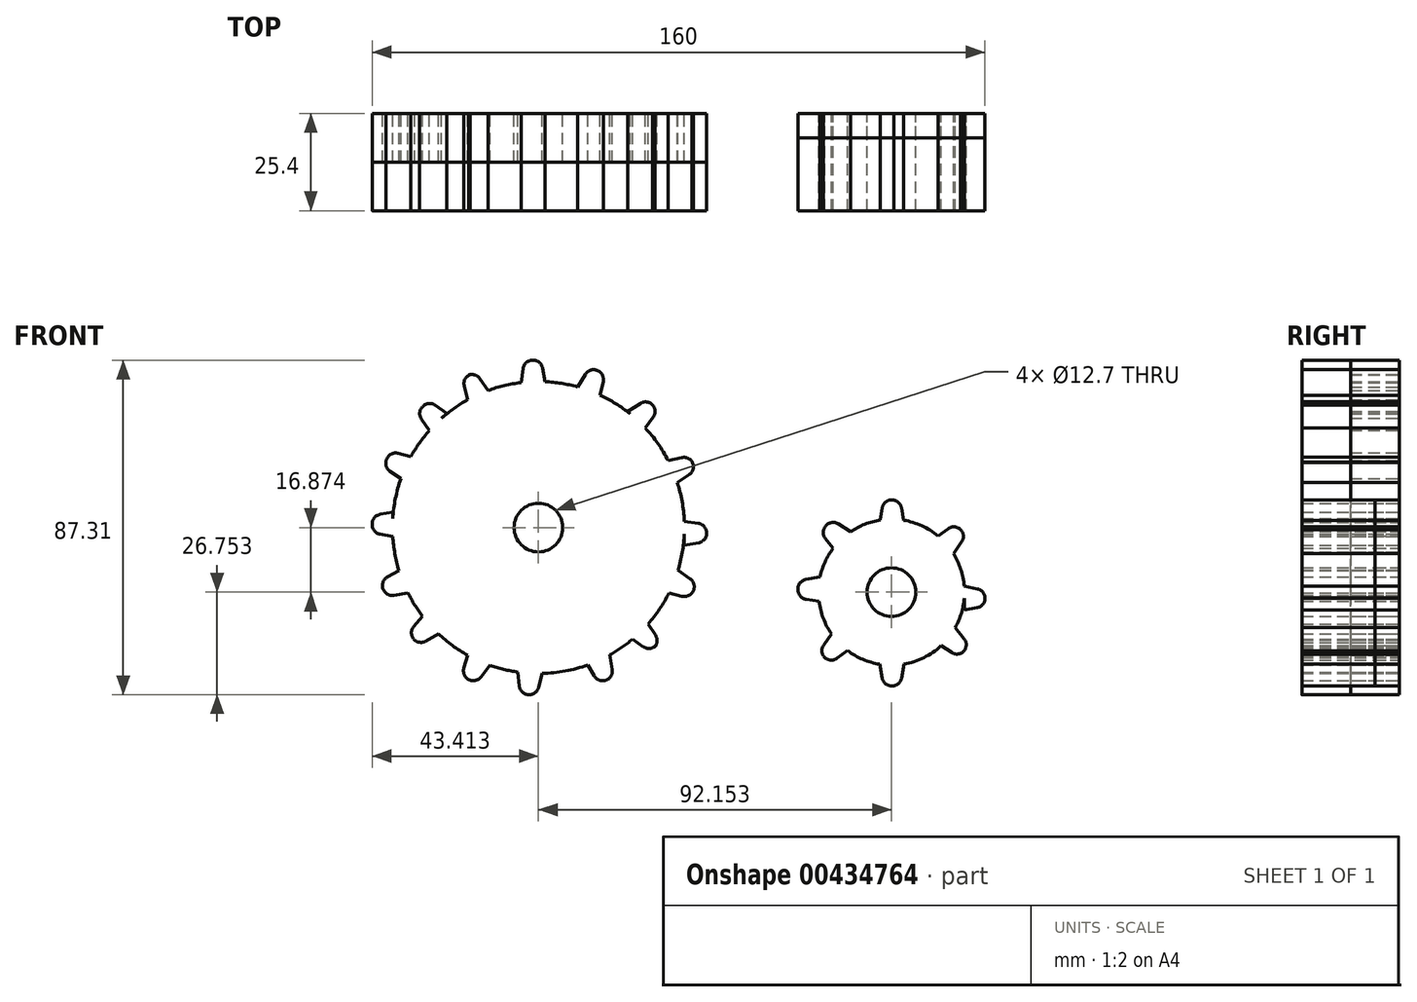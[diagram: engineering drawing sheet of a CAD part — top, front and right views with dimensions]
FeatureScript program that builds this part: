
annotation { "Feature Type Name" : "Feature", "Feature Type Description" : "" }
export const myFeature = defineFeature(function(context is Context, id is Id, definition is map)
    precondition{}
    {
        {
            var Q0;
            Q0=qCreatedBy(makeId("Front.planeOp"),FACE);
            var sketch = newSketch(context, id + "F0", { "sketchPlane" : qUnion([Q0])});
            skCircle(sketch, "E0", {"center": v(-53.1, 42.78) * mm, "radius": 38.1 * mm});
            skCircle(sketch, "E1", {"center": v(-53.1, 42.78) * mm, "radius": 6.35 * mm});
            skLineSegment(sketch, "E2", {"start": v(-57.08, 84.31) * mm, "end": v(-57.66, 80.6) * mm});
            skLineSegment(sketch, "E3", {"start": v(-51.35, 80.6) * mm, "end": v(-52.02, 84.36) * mm});
            skLineSegment(sketch, "E4", {"start": v(-54.55, 86.46) * mm, "end": v(-54.6, 86.46) * mm});
            skLineSegment(sketch, "E5", {"start": v(-57.66, 80.6) * mm, "end": v(-51.35, 80.6) * mm});
            skArc(sketch, "E6.filletArc", {"start": v(-54.6, 86.46) * mm, "mid": v(-56.23, 85.84) * mm, "end": v(-57.08, 84.31) * mm});
            skArc(sketch, "E7.filletArc", {"start": v(-52.02, 84.36) * mm, "mid": v(-52.9, 85.87) * mm, "end": v(-54.55, 86.46) * mm});
            skLineSegment(sketch, "E8", {"start": v(-94.4, 41.03) * mm, "end": v(-91.13, 40.45) * mm});
            skLineSegment(sketch, "E9", {"start": v(-91.13, 46.81) * mm, "end": v(-94.39, 46.24) * mm});
            skLineSegment(sketch, "E10", {"start": v(-96.48, 43.97) * mm, "end": v(-96.5, 43.77) * mm});
            skLineSegment(sketch, "E11", {"start": v(-91.13, 40.45) * mm, "end": v(-91.13, 46.81) * mm});
            skPoint(sketch, "E12.visualSharp", {"position": v(-96.71, 41.44) * mm});
            skArc(sketch, "E12.filletArc", {"start": v(-96.5, 43.77) * mm, "mid": v(-95.99, 42) * mm, "end": v(-94.4, 41.03) * mm});
            skPoint(sketch, "E13.visualSharp", {"position": v(-96.3, 45.9) * mm});
            skArc(sketch, "E13.filletArc", {"start": v(-94.39, 46.24) * mm, "mid": v(-95.81, 45.46) * mm, "end": v(-96.48, 43.97) * mm});
            skLineSegment(sketch, "E14", {"start": v(-26.55, 75.15) * mm, "end": v(-29.77, 73.06) * mm});
            skLineSegment(sketch, "E15", {"start": v(-25.48, 68.46) * mm, "end": v(-23.17, 71.52) * mm});
            skLineSegment(sketch, "E16", {"start": v(-23.33, 74.77) * mm, "end": v(-23.36, 74.8) * mm});
            skLineSegment(sketch, "E17", {"start": v(-29.77, 73.06) * mm, "end": v(-25.48, 68.46) * mm});
            skPoint(sketch, "E18.visualSharp", {"position": v(-24.78, 76.3) * mm});
            skArc(sketch, "E18.filletArc", {"start": v(-23.33, 74.77) * mm, "mid": v(-24.87, 75.54) * mm, "end": v(-26.55, 75.15) * mm});
            skPoint(sketch, "E19.visualSharp", {"position": v(-21.87, 73.25) * mm});
            skArc(sketch, "E19.filletArc", {"start": v(-23.17, 71.52) * mm, "mid": v(-22.66, 73.2) * mm, "end": v(-23.36, 74.8) * mm});
            skLineSegment(sketch, "E20", {"start": v(-82.5, 13.14) * mm, "end": v(-79.21, 15.04) * mm});
            skLineSegment(sketch, "E21", {"start": v(-83.24, 19.83) * mm, "end": v(-85.67, 16.93) * mm});
            skLineSegment(sketch, "E22", {"start": v(-85.44, 13.43) * mm, "end": v(-85.4, 13.39) * mm});
            skLineSegment(sketch, "E23", {"start": v(-79.21, 15.04) * mm, "end": v(-83.24, 19.83) * mm});
            skPoint(sketch, "E24.visualSharp", {"position": v(-84.07, 12.23) * mm});
            skArc(sketch, "E24.filletArc", {"start": v(-85.44, 13.43) * mm, "mid": v(-84.02, 12.81) * mm, "end": v(-82.5, 13.14) * mm});
            skPoint(sketch, "E25.visualSharp", {"position": v(-87.27, 15.03) * mm});
            skArc(sketch, "E25.filletArc", {"start": v(-85.67, 16.93) * mm, "mid": v(-86.25, 15.1) * mm, "end": v(-85.4, 13.39) * mm});
            skLineSegment(sketch, "E26", {"start": v(-15, 42.08) * mm, "end": v(-15, 41.4) * mm});
            skLineSegment(sketch, "E27", {"start": v(-83.64, 71.06) * mm, "end": v(-81.57, 68.1) * mm});
            skLineSegment(sketch, "E28", {"start": v(-77.06, 72.6) * mm, "end": v(-80.03, 74.68) * mm});
            skLineSegment(sketch, "E29", {"start": v(-83.3, 74.37) * mm, "end": v(-83.38, 74.3) * mm});
            skLineSegment(sketch, "E30", {"start": v(-81.57, 68.1) * mm, "end": v(-77.06, 72.6) * mm});
            skPoint(sketch, "E31.visualSharp", {"position": v(-84.85, 72.79) * mm});
            skArc(sketch, "E31.filletArc", {"start": v(-83.38, 74.3) * mm, "mid": v(-84.1, 72.72) * mm, "end": v(-83.64, 71.06) * mm});
            skPoint(sketch, "E32.visualSharp", {"position": v(-81.8, 75.91) * mm});
            skArc(sketch, "E32.filletArc", {"start": v(-80.03, 74.68) * mm, "mid": v(-81.72, 75.12) * mm, "end": v(-83.3, 74.37) * mm});
            skLineSegment(sketch, "E33", {"start": v(-22.56, 14.73) * mm, "end": v(-24.51, 17.59) * mm});
            skLineSegment(sketch, "E34", {"start": v(-28.51, 13.67) * mm, "end": v(-25.72, 11.67) * mm});
            skLineSegment(sketch, "E35", {"start": v(-22.81, 11.55) * mm, "end": v(-22.4, 12) * mm});
            skLineSegment(sketch, "E36", {"start": v(-24.51, 17.59) * mm, "end": v(-28.51, 13.67) * mm});
            skPoint(sketch, "E37.visualSharp", {"position": v(-21.4, 13.04) * mm});
            skArc(sketch, "E37.filletArc", {"start": v(-22.81, 11.55) * mm, "mid": v(-22.13, 13.1) * mm, "end": v(-22.56, 14.73) * mm});
            skPoint(sketch, "E38.visualSharp", {"position": v(-23.92, 10.38) * mm});
            skArc(sketch, "E38.filletArc", {"start": v(-25.72, 11.67) * mm, "mid": v(-24, 11.2) * mm, "end": v(-22.4, 12) * mm});
            skLineSegment(sketch, "E39", {"start": v(-40.85, 82.78) * mm, "end": v(-42.9, 79.49) * mm});
            skLineSegment(sketch, "E40", {"start": v(-37.01, 77.1) * mm, "end": v(-36.2, 80.9) * mm});
            skLineSegment(sketch, "E41", {"start": v(-37.76, 83.79) * mm, "end": v(-37.77, 83.8) * mm});
            skLineSegment(sketch, "E42", {"start": v(-42.9, 79.49) * mm, "end": v(-37.01, 77.1) * mm});
            skPoint(sketch, "E43.visualSharp", {"position": v(-39.73, 84.56) * mm});
            skArc(sketch, "E43.filletArc", {"start": v(-37.77, 83.8) * mm, "mid": v(-39.5, 83.84) * mm, "end": v(-40.85, 82.78) * mm});
            skPoint(sketch, "E44.visualSharp", {"position": v(-35.75, 83) * mm});
            skArc(sketch, "E44.filletArc", {"start": v(-36.2, 80.9) * mm, "mid": v(-36.45, 82.62) * mm, "end": v(-37.76, 83.79) * mm});
            skPoint(sketch, "E45.endSnap0", {"position": v(-92.76, 46.52) * mm});
            skLineSegment(sketch, "E46", {"start": v(-68.07, 3.83) * mm, "end": v(-65.78, 6.85) * mm});
            skLineSegment(sketch, "E47", {"start": v(-71.45, 9.76) * mm, "end": v(-72.57, 6.13) * mm});
            skLineSegment(sketch, "E48", {"start": v(-71.13, 3.05) * mm, "end": v(-71.09, 3.03) * mm});
            skLineSegment(sketch, "E49", {"start": v(-65.78, 6.85) * mm, "end": v(-71.45, 9.76) * mm});
            skPoint(sketch, "E50.visualSharp", {"position": v(-69.27, 2.25) * mm});
            skArc(sketch, "E50.filletArc", {"start": v(-71.09, 3.03) * mm, "mid": v(-69.44, 2.9) * mm, "end": v(-68.07, 3.83) * mm});
            skPoint(sketch, "E51.visualSharp", {"position": v(-73.25, 3.94) * mm});
            skArc(sketch, "E51.filletArc", {"start": v(-72.57, 6.13) * mm, "mid": v(-72.45, 4.31) * mm, "end": v(-71.13, 3.05) * mm});
            skLineSegment(sketch, "E52", {"start": v(-33.84, 5.77) * mm, "end": v(-34.5, 9.53) * mm});
            skLineSegment(sketch, "E53", {"start": v(-40.44, 7.36) * mm, "end": v(-38.54, 4.06) * mm});
            skLineSegment(sketch, "E54", {"start": v(-35.44, 2.95) * mm, "end": v(-35.44, 2.95) * mm});
            skLineSegment(sketch, "E55", {"start": v(-34.5, 9.53) * mm, "end": v(-40.44, 7.36) * mm});
            skPoint(sketch, "E56.visualSharp", {"position": v(-33.47, 3.7) * mm});
            skArc(sketch, "E56.filletArc", {"start": v(-35.44, 2.95) * mm, "mid": v(-34.13, 4.07) * mm, "end": v(-33.84, 5.77) * mm});
            skPoint(sketch, "E57.visualSharp", {"position": v(-37.46, 2.2) * mm});
            skArc(sketch, "E57.filletArc", {"start": v(-38.54, 4.06) * mm, "mid": v(-37.2, 2.94) * mm, "end": v(-35.44, 2.95) * mm});
            skLineSegment(sketch, "E58", {"start": v(-72.47, 79.7) * mm, "end": v(-71.54, 76.12) * mm});
            skLineSegment(sketch, "E59", {"start": v(-66.26, 78.53) * mm, "end": v(-68.39, 81.61) * mm});
            skLineSegment(sketch, "E60", {"start": v(-70.88, 82.73) * mm, "end": v(-71.35, 82.55) * mm});
            skLineSegment(sketch, "E61", {"start": v(-71.54, 76.12) * mm, "end": v(-66.26, 78.53) * mm});
            skPoint(sketch, "E62.visualSharp", {"position": v(-73.05, 81.93) * mm});
            skArc(sketch, "E62.filletArc", {"start": v(-70.88, 82.73) * mm, "mid": v(-72.26, 81.52) * mm, "end": v(-72.47, 79.7) * mm});
            skPoint(sketch, "E63.visualSharp", {"position": v(-69.5, 83.23) * mm});
            skArc(sketch, "E63.filletArc", {"start": v(-68.39, 81.61) * mm, "mid": v(-69.7, 82.59) * mm, "end": v(-71.35, 82.55) * mm});
            skLineSegment(sketch, "E64", {"start": v(-91.88, 57.5) * mm, "end": v(-89.01, 55.5) * mm});
            skLineSegment(sketch, "E65", {"start": v(-86.33, 61.25) * mm, "end": v(-89.7, 62.15) * mm});
            skLineSegment(sketch, "E66", {"start": v(-92.68, 60.75) * mm, "end": v(-92.73, 60.62) * mm});
            skLineSegment(sketch, "E67", {"start": v(-89.01, 55.5) * mm, "end": v(-86.33, 61.25) * mm});
            skPoint(sketch, "E68.visualSharp", {"position": v(-93.6, 58.7) * mm});
            skArc(sketch, "E68.filletArc", {"start": v(-92.73, 60.62) * mm, "mid": v(-92.87, 58.9) * mm, "end": v(-91.88, 57.5) * mm});
            skPoint(sketch, "E69.visualSharp", {"position": v(-91.79, 62.7) * mm});
            skArc(sketch, "E69.filletArc", {"start": v(-89.7, 62.15) * mm, "mid": v(-91.45, 62) * mm, "end": v(-92.68, 60.75) * mm});
            skLineSegment(sketch, "E70", {"start": v(-13.52, 29.42) * mm, "end": v(-16.67, 31.62) * mm});
            skLineSegment(sketch, "E71", {"start": v(-19.36, 25.84) * mm, "end": v(-15.65, 24.85) * mm});
            skLineSegment(sketch, "E72", {"start": v(-12.68, 26.25) * mm, "end": v(-12.66, 26.29) * mm});
            skLineSegment(sketch, "E73", {"start": v(-16.67, 31.62) * mm, "end": v(-19.36, 25.84) * mm});
            skPoint(sketch, "E74.visualSharp", {"position": v(-11.8, 28.2) * mm});
            skArc(sketch, "E74.filletArc", {"start": v(-12.66, 26.29) * mm, "mid": v(-12.53, 28) * mm, "end": v(-13.52, 29.42) * mm});
            skPoint(sketch, "E75.visualSharp", {"position": v(-13.57, 24.3) * mm});
            skArc(sketch, "E75.filletArc", {"start": v(-15.65, 24.85) * mm, "mid": v(-13.9, 25) * mm, "end": v(-12.68, 26.25) * mm});
            skLineSegment(sketch, "E76", {"start": v(-90.84, 25.08) * mm, "end": v(-87.15, 25.7) * mm});
            skLineSegment(sketch, "E77", {"start": v(-89.27, 31.68) * mm, "end": v(-92.52, 29.85) * mm});
            skLineSegment(sketch, "E78", {"start": v(-93.57, 26.53) * mm, "end": v(-93.54, 26.49) * mm});
            skLineSegment(sketch, "E79", {"start": v(-87.15, 25.7) * mm, "end": v(-89.27, 31.68) * mm});
            skPoint(sketch, "E80.visualSharp", {"position": v(-92.72, 24.77) * mm});
            skArc(sketch, "E80.filletArc", {"start": v(-93.54, 26.49) * mm, "mid": v(-92.42, 25.33) * mm, "end": v(-90.84, 25.08) * mm});
            skPoint(sketch, "E81.visualSharp", {"position": v(-94.6, 28.68) * mm});
            skArc(sketch, "E81.filletArc", {"start": v(-92.52, 29.85) * mm, "mid": v(-93.7, 28.4) * mm, "end": v(-93.57, 26.53) * mm});
            skLineSegment(sketch, "E82", {"start": v(-15.68, 61.02) * mm, "end": v(-19.23, 60.23) * mm});
            skLineSegment(sketch, "E83", {"start": v(-16.86, 54.56) * mm, "end": v(-13.82, 56.51) * mm});
            skLineSegment(sketch, "E84", {"start": v(-12.92, 59.79) * mm, "end": v(-12.98, 59.9) * mm});
            skLineSegment(sketch, "E85", {"start": v(-19.23, 60.23) * mm, "end": v(-16.86, 54.56) * mm});
            skPoint(sketch, "E86.visualSharp", {"position": v(-13.84, 61.43) * mm});
            skArc(sketch, "E86.filletArc", {"start": v(-12.92, 59.79) * mm, "mid": v(-14.1, 60.86) * mm, "end": v(-15.68, 61.02) * mm});
            skPoint(sketch, "E87.visualSharp", {"position": v(-11.8, 57.8) * mm});
            skArc(sketch, "E87.filletArc", {"start": v(-13.82, 56.51) * mm, "mid": v(-12.72, 58.04) * mm, "end": v(-12.98, 59.9) * mm});
            skLineSegment(sketch, "E88", {"start": v(-11.34, 43.85) * mm, "end": v(-15.03, 44.44) * mm});
            skLineSegment(sketch, "E89", {"start": v(-15.03, 38.13) * mm, "end": v(-11.3, 38.8) * mm});
            skLineSegment(sketch, "E90", {"start": v(-9.2, 41.32) * mm, "end": v(-9.2, 41.37) * mm});
            skLineSegment(sketch, "E91", {"start": v(-15.03, 44.44) * mm, "end": v(-15.03, 38.13) * mm});
            skArc(sketch, "E92.filletArc", {"start": v(-9.2, 41.37) * mm, "mid": v(-9.81, 43) * mm, "end": v(-11.34, 43.85) * mm});
            skArc(sketch, "E93.filletArc", {"start": v(-11.3, 38.8) * mm, "mid": v(-9.78, 39.67) * mm, "end": v(-9.2, 41.32) * mm});
            skLineSegment(sketch, "E94", {"start": v(-53.07, 1.08) * mm, "end": v(-52.18, 4.69) * mm});
            skLineSegment(sketch, "E95", {"start": v(-58.45, 5.24) * mm, "end": v(-58.12, 1.48) * mm});
            skLineSegment(sketch, "E96", {"start": v(-55.78, -0.84) * mm, "end": v(-55.73, -0.84) * mm});
            skLineSegment(sketch, "E97", {"start": v(-52.18, 4.69) * mm, "end": v(-58.45, 5.24) * mm});
            skArc(sketch, "E98.filletArc", {"start": v(-55.73, -0.84) * mm, "mid": v(-54.05, -0.37) * mm, "end": v(-53.07, 1.08) * mm});
            skArc(sketch, "E99.filletArc", {"start": v(-58.12, 1.48) * mm, "mid": v(-57.38, -0.1) * mm, "end": v(-55.78, -0.84) * mm});
            skSolve(sketch);
        }
        {
            var Q0;
            Q0 = qSketchRegion(id + "F0", true);
            extrude(context, id + "F1", {"entities" : qUnion([Q0]), "depth" : 12.7 * mm});
        }
        {
            var Q0;
            Q0=qCreatedBy(makeId("Front.planeOp"),FACE);
            var sketch = newSketch(context, id + "F2", { "sketchPlane" : qUnion([Q0])});
            skCircle(sketch, "E100", {"center": v(39.06, 25.9) * mm, "radius": 19.05 * mm});
            skCircle(sketch, "E101", {"center": v(39.06, 25.9) * mm, "radius": 6.35 * mm});
            skLineSegment(sketch, "E102", {"start": v(36.67, 47.92) * mm, "end": v(36.09, 44.72) * mm});
            skLineSegment(sketch, "E103", {"start": v(42.2, 44.7) * mm, "end": v(41.66, 47.9) * mm});
            skLineSegment(sketch, "E104", {"start": v(39.73, 49.94) * mm, "end": v(39.72, 49.95) * mm});
            skLineSegment(sketch, "E105", {"start": v(36.09, 44.72) * mm, "end": v(42.2, 44.7) * mm});
            skArc(sketch, "E106.filletArc", {"start": v(39.73, 49.94) * mm, "mid": v(37.77, 49.59) * mm, "end": v(36.67, 47.92) * mm});
            skPoint(sketch, "E107.visualSharp", {"position": v(40.78, 63.59) * mm});
            skArc(sketch, "E107.filletArc", {"start": v(41.66, 47.9) * mm, "mid": v(41, 49.22) * mm, "end": v(39.72, 49.95) * mm});
            skLineSegment(sketch, "E108", {"start": v(41.69, 3.54) * mm, "end": v(42.3, 7.13) * mm});
            skLineSegment(sketch, "E109", {"start": v(36, 7.1) * mm, "end": v(36.64, 3.52) * mm});
            skLineSegment(sketch, "E110", {"start": v(38.9, 1.44) * mm, "end": v(38.95, 1.44) * mm});
            skLineSegment(sketch, "E111", {"start": v(42.3, 7.13) * mm, "end": v(36, 7.1) * mm});
            skPoint(sketch, "E112.visualSharp", {"position": v(41.3, 1.23) * mm});
            skArc(sketch, "E112.filletArc", {"start": v(38.95, 1.44) * mm, "mid": v(40.73, 1.96) * mm, "end": v(41.69, 3.54) * mm});
            skPoint(sketch, "E113.visualSharp", {"position": v(36.98, 1.62) * mm});
            skArc(sketch, "E113.filletArc", {"start": v(36.64, 3.52) * mm, "mid": v(37.42, 2.1) * mm, "end": v(38.9, 1.44) * mm});
            skLineSegment(sketch, "E114", {"start": v(36, 7.1) * mm, "end": v(39.06, 7.49) * mm});
            skLineSegment(sketch, "E115", {"start": v(39.06, 25.9) * mm, "end": v(39.06, 21.65) * mm});
            skLineSegment(sketch, "E116", {"start": v(39.06, 25.9) * mm, "end": v(39.06, 30.09) * mm});
            skLineSegment(sketch, "E117", {"start": v(4.99, 41.49) * mm, "end": v(9.44, 41.49) * mm});
            skLineSegment(sketch, "E118", {"start": v(17.84, 46.87) * mm, "end": v(22.3, 46.87) * mm});
            skLineSegment(sketch, "E119", {"start": v(16.79, 24.04) * mm, "end": v(20.49, 23.45) * mm});
            skLineSegment(sketch, "E120", {"start": v(20.49, 29.9) * mm, "end": v(16.74, 29.23) * mm});
            skLineSegment(sketch, "E121", {"start": v(14.64, 26.7) * mm, "end": v(14.64, 26.52) * mm});
            skLineSegment(sketch, "E122", {"start": v(20.49, 23.45) * mm, "end": v(20.49, 29.9) * mm});
            skArc(sketch, "E123.filletArc", {"start": v(14.64, 26.52) * mm, "mid": v(15.26, 24.89) * mm, "end": v(16.79, 24.04) * mm});
            skArc(sketch, "E124.filletArc", {"start": v(16.74, 29.23) * mm, "mid": v(15.22, 28.35) * mm, "end": v(14.64, 26.7) * mm});
            skLineSegment(sketch, "E125", {"start": v(61.47, 26.78) * mm, "end": v(58.04, 27.5) * mm});
            skLineSegment(sketch, "E126", {"start": v(58.04, 21.26) * mm, "end": v(61.39, 21.85) * mm});
            skLineSegment(sketch, "E127", {"start": v(63.49, 24.32) * mm, "end": v(63.49, 24.38) * mm});
            skLineSegment(sketch, "E128", {"start": v(58.04, 27.5) * mm, "end": v(58.04, 21.26) * mm});
            skArc(sketch, "E129.filletArc", {"start": v(63.49, 24.32) * mm, "mid": v(62.91, 25.9) * mm, "end": v(61.47, 26.78) * mm});
            skArc(sketch, "E130.filletArc", {"start": v(61.39, 21.85) * mm, "mid": v(62.9, 22.73) * mm, "end": v(63.49, 24.38) * mm});
            skLineSegment(sketch, "E131", {"start": v(24.84, 8.67) * mm, "end": v(27.6, 10.68) * mm});
            skLineSegment(sketch, "E132", {"start": v(23.53, 15.2) * mm, "end": v(21.35, 12.1) * mm});
            skLineSegment(sketch, "E133", {"start": v(21.57, 8.91) * mm, "end": v(21.66, 8.83) * mm});
            skLineSegment(sketch, "E134", {"start": v(27.6, 10.68) * mm, "end": v(23.53, 15.2) * mm});
            skArc(sketch, "E135.filletArc", {"start": v(21.57, 8.91) * mm, "mid": v(23.16, 8.2) * mm, "end": v(24.84, 8.67) * mm});
            skArc(sketch, "E136.filletArc", {"start": v(21.35, 12.1) * mm, "mid": v(20.9, 10.4) * mm, "end": v(21.66, 8.83) * mm});
            skLineSegment(sketch, "E137", {"start": v(58.03, 13.77) * mm, "end": v(55.73, 16.7) * mm});
            skLineSegment(sketch, "E138", {"start": v(51.57, 12.2) * mm, "end": v(54.74, 10.16) * mm});
            skLineSegment(sketch, "E139", {"start": v(57.91, 10.5) * mm, "end": v(58, 10.58) * mm});
            skLineSegment(sketch, "E140", {"start": v(55.73, 16.7) * mm, "end": v(51.57, 12.2) * mm});
            skArc(sketch, "E141.filletArc", {"start": v(57.91, 10.5) * mm, "mid": v(58.57, 12.1) * mm, "end": v(58.03, 13.77) * mm});
            skArc(sketch, "E142.filletArc", {"start": v(54.74, 10.16) * mm, "mid": v(56.44, 9.77) * mm, "end": v(58, 10.58) * mm});
            skLineSegment(sketch, "E143", {"start": v(53.85, 42.47) * mm, "end": v(51.22, 40.56) * mm});
            skLineSegment(sketch, "E144", {"start": v(55.2, 35.88) * mm, "end": v(57.39, 39) * mm});
            skLineSegment(sketch, "E145", {"start": v(57.12, 42.24) * mm, "end": v(57.08, 42.27) * mm});
            skLineSegment(sketch, "E146", {"start": v(51.22, 40.56) * mm, "end": v(55.2, 35.88) * mm});
            skArc(sketch, "E147.filletArc", {"start": v(57.12, 42.24) * mm, "mid": v(55.53, 42.95) * mm, "end": v(53.85, 42.47) * mm});
            skArc(sketch, "E148.filletArc", {"start": v(57.39, 39) * mm, "mid": v(57.84, 40.7) * mm, "end": v(57.08, 42.27) * mm});
            skLineSegment(sketch, "E149", {"start": v(21.8, 39.93) * mm, "end": v(23.84, 37.37) * mm});
            skLineSegment(sketch, "E150", {"start": v(28.41, 41.67) * mm, "end": v(25.2, 43.72) * mm});
            skLineSegment(sketch, "E151", {"start": v(21.94, 43.27) * mm, "end": v(21.9, 43.2) * mm});
            skLineSegment(sketch, "E152", {"start": v(23.84, 37.37) * mm, "end": v(28.41, 41.67) * mm});
            skArc(sketch, "E153.filletArc", {"start": v(21.9, 43.2) * mm, "mid": v(21.25, 41.58) * mm, "end": v(21.8, 39.93) * mm});
            skArc(sketch, "E154.filletArc", {"start": v(25.2, 43.72) * mm, "mid": v(23.49, 44.09) * mm, "end": v(21.94, 43.27) * mm});
            skLineSegment(sketch, "E155", {"start": v(-46.68, -23.66) * mm, "end": v(-46.68, -27.92) * mm});
            skSolve(sketch);
        }
        {
            var Q0;
            Q0 = qSketchRegion(id + "F2", true);
            extrude(context, id + "F3", {"entities" : qUnion([Q0]), "depth" : 6.35 * mm});
        }
        {
            var Q0;
            Q0 = qSketchRegion(id + "F0", true);
            extrude(context, id + "F4", {"entities" : qUnion([Q0]), "operationType" : NewBodyOperationType.ADD, "depth" : 25.4 * mm});
        }
        {
            var Q0;
            Q0 = qSketchRegion(id + "F2", true);
            extrude(context, id + "F5", {"entities" : qUnion([Q0]), "operationType" : NewBodyOperationType.ADD, "depth" : 25.4 * mm});
        }
    });
